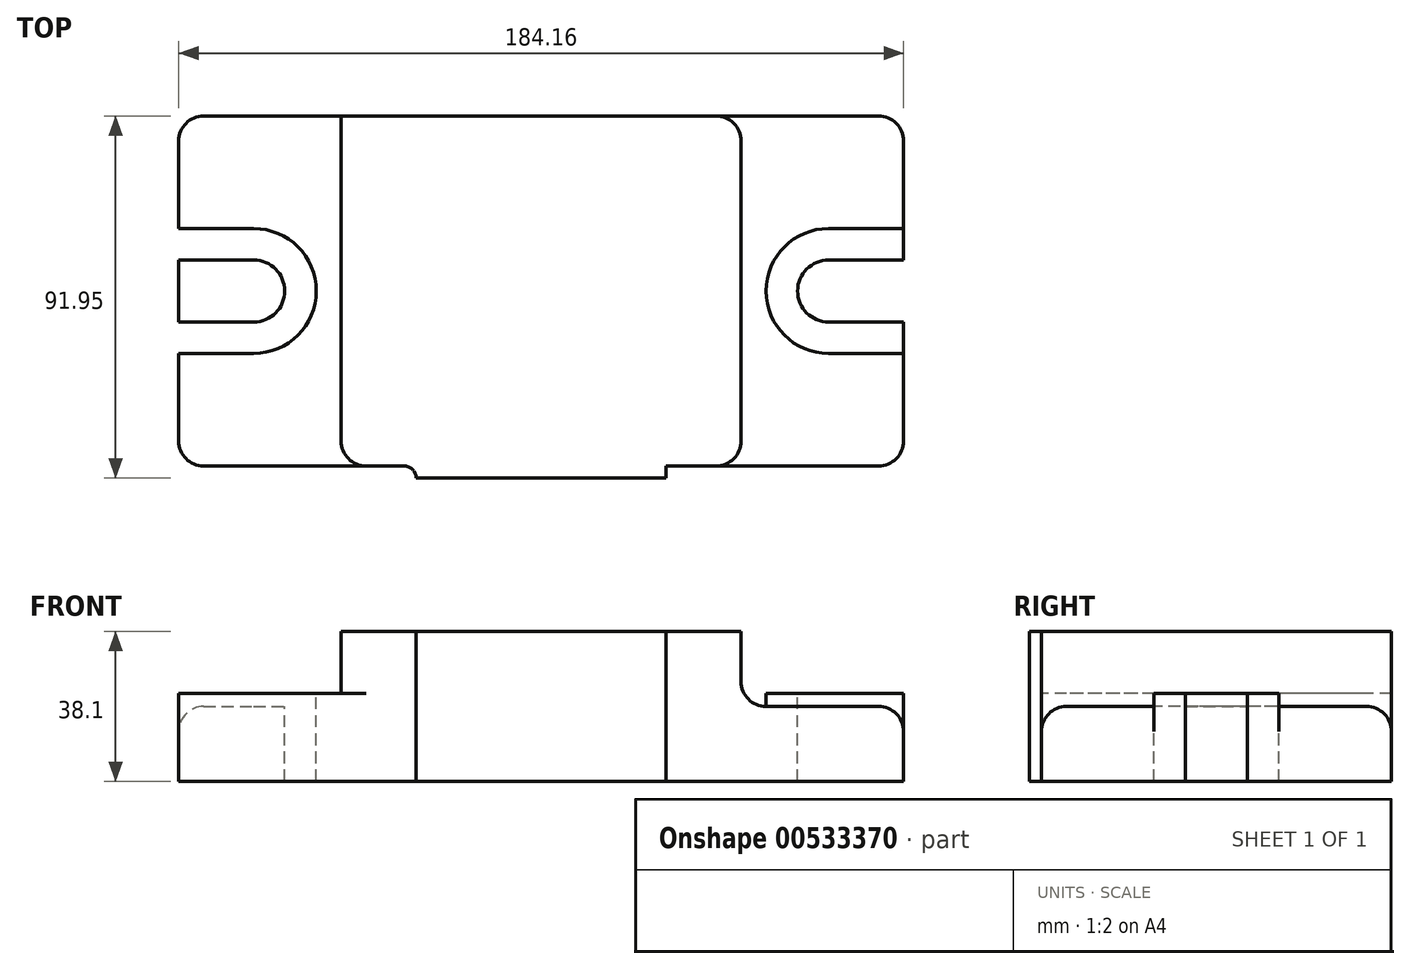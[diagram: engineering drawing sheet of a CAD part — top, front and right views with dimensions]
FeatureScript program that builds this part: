
annotation { "Feature Type Name" : "Feature", "Feature Type Description" : "" }
export const myFeature = defineFeature(function(context is Context, id is Id, definition is map)
    precondition{}
    {
        {
            var Q0;
            Q0=qCreatedBy(makeId("Front.planeOp"),FACE);
            var sketch = newSketch(context, id + "F0", { "sketchPlane" : qUnion([Q0])});
            skLineSegment(sketch, "E0", {"start": v(-92.08, 0) * mm, "end": v(92.08, 0) * mm});
            skPoint(sketch, "E1", {"position": v(0, 0) * mm});
            skLineSegment(sketch, "E2.0", {"start": v(-50.8, 38.1) * mm, "end": v(50.8, 38.1) * mm});
            skLineSegment(sketch, "E3.0", {"start": v(-92.08, 19.05) * mm, "end": v(-50.8, 19.05) * mm});
            skLineSegment(sketch, "E4", {"start": v(-92.08, 19.05) * mm, "end": v(-92.08, 0) * mm});
            skLineSegment(sketch, "E5", {"start": v(92.08, 19.05) * mm, "end": v(92.08, 0) * mm});
            skPoint(sketch, "E6", {"position": v(0, 38.1) * mm});
            skLineSegment(sketch, "E7", {"start": v(-50.8, 38.1) * mm, "end": v(-50.8, 19.05) * mm});
            skLineSegment(sketch, "E8", {"start": v(50.8, 38.1) * mm, "end": v(50.8, 19.05) * mm});
            skLineSegment(sketch, "E9.trimOffspring", {"start": v(50.8, 19.05) * mm, "end": v(92.08, 19.05) * mm});
            skSolve(sketch);
        }
        {
            var Q0;
            Q0=makeQuery(id+"F0.imprint","IMPRINT",FACE,{"disambiguationData":[TD([[makeQuery(id+"F0.imprint","IMPRINT",EDGE,{"derivedFrom":sQuery(id+"F0.wireOp",EDGE,"E0")}),1.0]])]});
            extrude(context, id + "F1", {"entities" : qUnion([Q0]), "oppositeDirection" : true, "depth" : 88.9 * mm, "offsetDistance" : 25.4 * mm});
        }
        {
            var Q0;
            Q0=makeQuery(id+"F1.opExtrude","SWEPT_FACE",FACE,{"disambiguationData":[OSD([sQuery(id+"F0.wireOp",EDGE,"E3.0")])]});
            var sketch = newSketch(context, id + "F2", { "sketchPlane" : qUnion([Q0])});
            skLineSegment(sketch, "E10", {"start": v(-92.08, 44.45) * mm, "end": v(-73.03, 44.45) * mm, "construction": true});
            skPoint(sketch, "E11", {"position": v(-92.08, 44.45) * mm});
            skLineSegment(sketch, "E12", {"start": v(0, 0) * mm, "end": v(0, 123.68) * mm, "construction": true});
            skArc(sketch, "E13.0.startCap", {"start": v(-92.08, 28.58) * mm, "mid": v(-107.95, 44.45) * mm, "end": v(-92.08, 60.33) * mm});
            skArc(sketch, "E13.0.endCap", {"start": v(-73.03, 60.33) * mm, "mid": v(-57.15, 44.45) * mm, "end": v(-73.03, 28.58) * mm});
            skLineSegment(sketch, "E13.0.left", {"start": v(-92.08, 60.32) * mm, "end": v(-73.03, 60.32) * mm});
            skLineSegment(sketch, "E13.0.right", {"start": v(-92.08, 28.58) * mm, "end": v(-73.03, 28.58) * mm});
            skArc(sketch, "E14.0.startCap", {"start": v(-92.08, 36.58) * mm, "mid": v(-99.95, 44.45) * mm, "end": v(-92.08, 52.32) * mm});
            skArc(sketch, "E14.0.endCap", {"start": v(-73.03, 52.32) * mm, "mid": v(-65.15, 44.45) * mm, "end": v(-73.03, 36.58) * mm});
            skLineSegment(sketch, "E14.0.left", {"start": v(-92.08, 52.32) * mm, "end": v(-73.03, 52.32) * mm});
            skLineSegment(sketch, "E14.0.right", {"start": v(-92.08, 36.58) * mm, "end": v(-73.03, 36.58) * mm});
            skLineSegment(sketch, "E15.MirrorCS", {"start": v(92.08, 52.32) * mm, "end": v(73.03, 52.32) * mm});
            skLineSegment(sketch, "E16.MirrorCS", {"start": v(92.08, 60.32) * mm, "end": v(73.03, 60.32) * mm});
            skArc(sketch, "E17.MirrorCS", {"start": v(73.03, 60.33) * mm, "mid": v(57.15, 44.45) * mm, "end": v(73.03, 28.58) * mm});
            skArc(sketch, "E18.MirrorCS", {"start": v(92.08, 28.58) * mm, "mid": v(107.95, 44.45) * mm, "end": v(92.08, 60.33) * mm});
            skLineSegment(sketch, "E19.MirrorCS", {"start": v(92.08, 36.58) * mm, "end": v(73.03, 36.58) * mm});
            skLineSegment(sketch, "E20.MirrorCS", {"start": v(92.08, 44.45) * mm, "end": v(73.03, 44.45) * mm, "construction": true});
            skArc(sketch, "E21.MirrorCS", {"start": v(92.08, 36.58) * mm, "mid": v(99.95, 44.45) * mm, "end": v(92.08, 52.32) * mm});
            skLineSegment(sketch, "E22.MirrorCS", {"start": v(92.08, 28.58) * mm, "end": v(73.03, 28.58) * mm});
            skArc(sketch, "E23.MirrorCS", {"start": v(73.03, 52.32) * mm, "mid": v(65.15, 44.45) * mm, "end": v(73.03, 36.58) * mm});
            skLineSegment(sketch, "E24", {"start": v(92.08, 60.32) * mm, "end": v(92.08, 52.32) * mm});
            skLineSegment(sketch, "E25", {"start": v(92.08, 36.58) * mm, "end": v(92.08, 28.58) * mm});
            skSolve(sketch);
        }
        {
            var Q0;
            Q0=makeQuery(id+"F2.imprint","IMPRINT",FACE,{"disambiguationData":[TD([[makeQuery(id+"F2.imprint","IMPRINT",EDGE,{"derivedFrom":sQuery(id+"F2.wireOp",EDGE,"E14.0.endCap")}),-1.0]])]});
            var Q1;
            Q1=makeQuery(id+"F2.imprint","IMPRINT",FACE,{"disambiguationData":[TD([[makeQuery(id+"F2.imprint","IMPRINT",EDGE,{"derivedFrom":sQuery(id+"F2.wireOp",EDGE,"E15.MirrorCS")}),1.0]])]});
            extrude(context, id + "F3", {"entities" : qUnion([Q0, Q1]), "operationType" : NewBodyOperationType.REMOVE, "endBound" : BoundingType.UP_TO_NEXT, "oppositeDirection" : true, "depth" : 25.4 * mm, "offsetDistance" : 25.4 * mm});
        }
        {
            var Q0;
            Q0=makeQuery(id+"F2.imprint","IMPRINT",FACE,{"disambiguationData":[TD([[makeQuery(id+"F2.imprint","IMPRINT",EDGE,{"derivedFrom":sQuery(id+"F2.wireOp",EDGE,"E13.0.endCap")}),-1.0]])]});
            var Q1;
            Q1=makeQuery(id+"F2.imprint","IMPRINT",FACE,{"disambiguationData":[TD([[makeQuery(id+"F2.imprint","IMPRINT",EDGE,{"derivedFrom":sQuery(id+"F2.wireOp",EDGE,"E15.MirrorCS")}),-1.0]])]});
            extrude(context, id + "F4", {"entities" : qUnion([Q0, Q1]), "operationType" : NewBodyOperationType.ADD, "depth" : 3.3 * mm, "offsetDistance" : 25.4 * mm});
        }
        {
            var Q0;
            Q0=makeQuery(id+"F1.opExtrude","CAP_FACE",FACE,{"disambiguationData":[OSD([sQuery(id+"F0.wireOp",EDGE,"E0"),sQuery(id+"F0.wireOp",EDGE,"E2.0"),sQuery(id+"F0.wireOp",EDGE,"E3.0"),sQuery(id+"F0.wireOp",EDGE,"E4"),sQuery(id+"F0.wireOp",EDGE,"E5"),sQuery(id+"F0.wireOp",EDGE,"E7"),sQuery(id+"F0.wireOp",EDGE,"E8"),sQuery(id+"F0.wireOp",EDGE,"E9.trimOffspring")])],"isStart":true});
            var sketch = newSketch(context, id + "F5", { "sketchPlane" : qUnion([Q0])});
            skLineSegment(sketch, "E26.bottom", {"start": v(-31.75, 0) * mm, "end": v(31.75, 0) * mm});
            skLineSegment(sketch, "E26.top", {"start": v(-31.75, 38.1) * mm, "end": v(31.75, 38.1) * mm});
            skLineSegment(sketch, "E26.left", {"start": v(-31.75, 0) * mm, "end": v(-31.75, 38.1) * mm});
            skLineSegment(sketch, "E26.right", {"start": v(31.75, 0) * mm, "end": v(31.75, 38.1) * mm});
            skPoint(sketch, "E27", {"position": v(0, 0) * mm});
            skSolve(sketch);
        }
        {
            var Q0;
            Q0 = qSketchRegion(id + "F5", true);
            extrude(context, id + "F6", {"entities" : qUnion([Q0]), "operationType" : NewBodyOperationType.ADD, "depth" : 3.05 * mm, "offsetDistance" : 25.4 * mm});
        }
        {
            var Q0;
            Q0=makeQuery(id+"F1.opExtrude","CAP_EDGE",EDGE,{"disambiguationData":[OSD([sQuery(id+"F0.wireOp",EDGE,"E4")])],"isStart":true});
            var Q1;
            Q1=makeQuery(id+"F1.opExtrude","CAP_EDGE",EDGE,{"disambiguationData":[OSD([sQuery(id+"F0.wireOp",EDGE,"E3.0")])],"isStart":true});
            var Q2;
            Q2=makeQuery(id+"F1.opExtrude","CAP_EDGE",EDGE,{"disambiguationData":[OSD([sQuery(id+"F0.wireOp",EDGE,"E7")])],"isStart":true});
            var Q3;
            Q3=makeQuery(id+"F1.opExtrude","SWEPT_EDGE",EDGE,{"disambiguationData":[OSD([sQuery(id+"F0.wireOp",EDGE,"E3.0"),sQuery(id+"F0.wireOp",EDGE,"E7")])]});
            var Q4;
            Q4=makeQuery(id+"F1.opExtrude","CAP_EDGE",EDGE,{"disambiguationData":[OSD([sQuery(id+"F0.wireOp",EDGE,"E4")])],"isStart":false});
            var Q5;
            Q5=makeQuery(id+"F1.opExtrude","CAP_EDGE",EDGE,{"disambiguationData":[OSD([sQuery(id+"F0.wireOp",EDGE,"E3.0")])],"isStart":false});
            var Q6;
            {var subQ0=sQuery(id+"F0.wireOp",EDGE,"E4");var subQ1=sQuery(id+"F0.wireOp",EDGE,"E3.0");Q6=makeQuery(id+"F3.boolean.opBoolean","SPLIT",EDGE,{"disambiguationData":[TD([makeQuery(id+"F3.opExtrude","SWEPT_FACE",FACE,{"disambiguationData":[OSD([sQuery(id+"F2.wireOp",EDGE,"E14.0.left")])]})])],"derivedFrom":makeQuery(id+"F1.opExtrude","SWEPT_EDGE",EDGE,{"disambiguationData":[OSD([subQ1,subQ0])]})});}
            var Q7;
            {var subQ0=sQuery(id+"F0.wireOp",EDGE,"E4");var subQ1=sQuery(id+"F0.wireOp",EDGE,"E3.0");Q7=makeQuery(id+"F3.boolean.opBoolean","SPLIT",EDGE,{"disambiguationData":[TD([makeQuery(id+"F3.opExtrude","SWEPT_FACE",FACE,{"disambiguationData":[OSD([sQuery(id+"F2.wireOp",EDGE,"E14.0.right")])]})])],"derivedFrom":makeQuery(id+"F1.opExtrude","SWEPT_EDGE",EDGE,{"disambiguationData":[OSD([subQ1,subQ0])]})});}
            var Q8;
            Q8=makeQuery(id+"F1.opExtrude","CAP_EDGE",EDGE,{"disambiguationData":[OSD([sQuery(id+"F0.wireOp",EDGE,"E8")])],"isStart":false});
            var Q9;
            Q9=makeQuery(id+"F1.opExtrude","CAP_EDGE",EDGE,{"disambiguationData":[OSD([sQuery(id+"F0.wireOp",EDGE,"E9.trimOffspring")])],"isStart":false});
            var Q10;
            Q10=makeQuery(id+"F1.opExtrude","SWEPT_EDGE",EDGE,{"disambiguationData":[OSD([sQuery(id+"F0.wireOp",EDGE,"E8"),sQuery(id+"F0.wireOp",EDGE,"E9.trimOffspring")])]});
            var Q11;
            Q11=makeQuery(id+"F1.opExtrude","CAP_EDGE",EDGE,{"disambiguationData":[OSD([sQuery(id+"F0.wireOp",EDGE,"E5")])],"isStart":false});
            var Q12;
            {var subQ0=sQuery(id+"F0.wireOp",EDGE,"E9.trimOffspring");var subQ1=sQuery(id+"F0.wireOp",EDGE,"E5");Q12=makeQuery(id+"F3.boolean.opBoolean","SPLIT",EDGE,{"disambiguationData":[TD([makeQuery(id+"F3.opExtrude","SWEPT_FACE",FACE,{"disambiguationData":[OSD([sQuery(id+"F2.wireOp",EDGE,"E15.MirrorCS")])]})])],"derivedFrom":makeQuery(id+"F1.opExtrude","SWEPT_EDGE",EDGE,{"disambiguationData":[OSD([subQ1,subQ0])]})});}
            var Q13;
            {var subQ0=sQuery(id+"F0.wireOp",EDGE,"E9.trimOffspring");var subQ1=sQuery(id+"F0.wireOp",EDGE,"E5");Q13=makeQuery(id+"F3.boolean.opBoolean","SPLIT",EDGE,{"disambiguationData":[TD([makeQuery(id+"F3.opExtrude","SWEPT_FACE",FACE,{"disambiguationData":[OSD([sQuery(id+"F2.wireOp",EDGE,"E19.MirrorCS")])]})])],"derivedFrom":makeQuery(id+"F1.opExtrude","SWEPT_EDGE",EDGE,{"disambiguationData":[OSD([subQ1,subQ0])]})});}
            var Q14;
            Q14=makeQuery(id+"F1.opExtrude","CAP_EDGE",EDGE,{"disambiguationData":[OSD([sQuery(id+"F0.wireOp",EDGE,"E9.trimOffspring")])],"isStart":true});
            var Q15;
            Q15=makeQuery(id+"F1.opExtrude","CAP_EDGE",EDGE,{"disambiguationData":[OSD([sQuery(id+"F0.wireOp",EDGE,"E8")])],"isStart":true});
            var Q16;
            Q16=makeQuery(id+"F1.opExtrude","CAP_EDGE",EDGE,{"disambiguationData":[OSD([sQuery(id+"F0.wireOp",EDGE,"E5")])],"isStart":true});
            fillet(context, id + "F7", {"entities" : qUnion([Q0, Q1, Q2, Q3, Q4, Q5, Q6, Q7, Q8, Q9, Q10, Q11, Q12, Q13, Q14, Q15, Q16]), "radius" : 6.35 * mm, "tangentPropagation" : true, "allowEdgeOverflow" : false});
        }
        {
            var Q0;
            Q0=makeQuery(id+"F4.opExtrude","CAP_EDGE",EDGE,{"disambiguationData":[OSD([sQuery(id+"F2.wireOp",EDGE,"E16.MirrorCS")])],"isStart":true});
            var Q1;
            Q1=makeQuery(id+"F4.opExtrude","CAP_EDGE",EDGE,{"disambiguationData":[OSD([sQuery(id+"F2.wireOp",EDGE,"E13.0.left")])],"isStart":true});
            var Q2;
            Q2=makeQuery(id+"F6.opExtrude","CAP_EDGE",EDGE,{"disambiguationData":[OSD([sQuery(id+"F5.wireOp",EDGE,"E26.left")])],"isStart":true});
            var Q3;
            Q3=makeQuery(id+"F6.opExtrude","CAP_EDGE",EDGE,{"disambiguationData":[OSD([sQuery(id+"F5.wireOp",EDGE,"E26.right")])],"isStart":true});
            fillet(context, id + "F8", {"entities" : qUnion([Q0, Q1, Q2, Q3]), "radius" : 3.17 * mm, "tangentPropagation" : true, "allowEdgeOverflow" : false});
        }
    });
